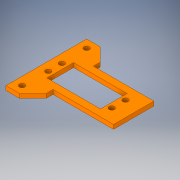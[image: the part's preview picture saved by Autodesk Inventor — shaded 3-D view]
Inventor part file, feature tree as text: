
AUTODESK INVENTOR PART (.ipt)
format: ipt  version: 2019 (Build 230136000, 136)  size: 158,208 bytes
history: native  units: mm
features: chamfer x2, extrude x1, sketch x1
ambient origin geometry x8: Origin, YZ Plane, XZ Plane, XY Plane, X Axis, Y Axis, Z Axis, Center Point
bodies: Body1 (feature_tree)
feature tree (4):
  extrude  "Extrusion2"  Depth=2.0mm
  chamfer  "Chamfer1"  Distance=4.0mm
  chamfer  "Chamfer2"  Distance=5.085mm
  sketch  "Sketch2"  dims[d27=4.0mm d28=4.0mm d29=4.0mm d30=4.0mm d31=13.47mm d32=5.085mm d33=10.17mm d34=13.47mm d35=33.79mm d36=5.085mm d37=10.17mm d38=33.79mm d39=30.0mm d40=65.0mm d41=20.0mm d42=15.0mm d43=60.0mm d44=30.0mm d45=20.0mm d46=4.0mm d47=4.0mm d48=6.0mm d49=6.0mm d50=6.0mm d51=6.0mm d52=9.66mm d53=19.82mm d54=9.91mm d55=39.88mm d56=3.18mm d57=0.0mm d58=10.0mm d59=2.0mm d60=45.0deg d61=10.0mm d62=2.0mm d63=45.0deg]
